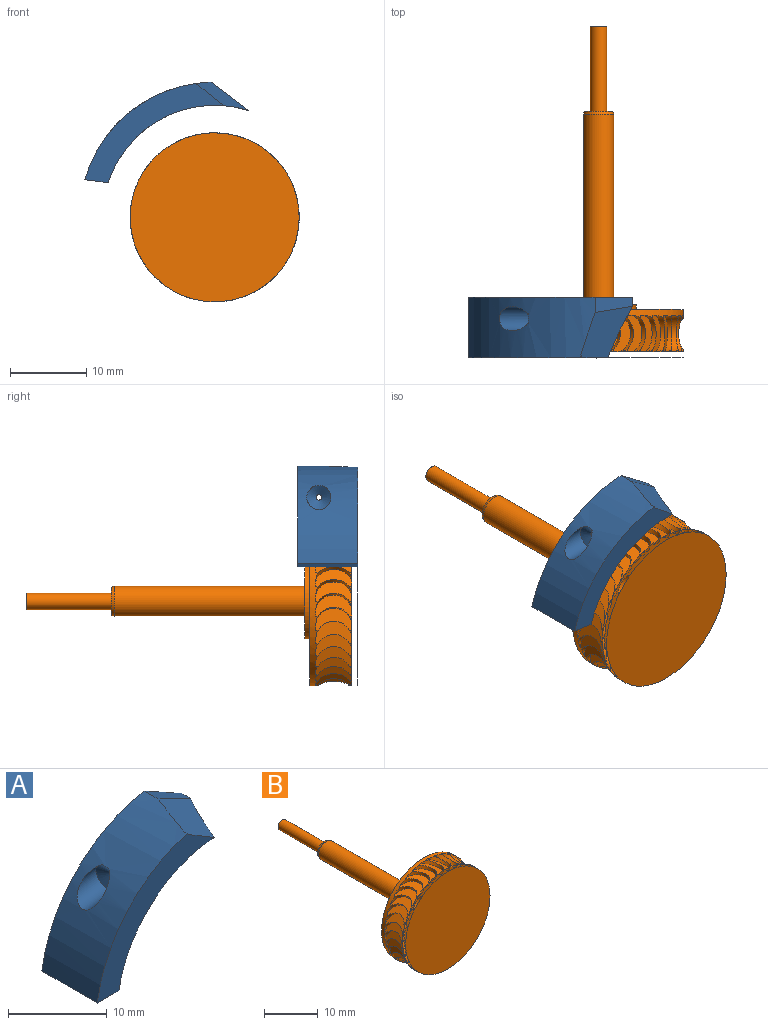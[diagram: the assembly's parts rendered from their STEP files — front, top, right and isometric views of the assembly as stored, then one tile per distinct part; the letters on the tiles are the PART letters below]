
ASSEMBLY  parts=2 mates=2
PART A: 42 faces, bbox 20.2x8.1x15.2 mm
  f0: plane 16.73x14.61mm, normal (0,-1,0), area 61mm2, adj f1,f2,f38,f40,f41
  f1: cylinder r=17.78mm len=15mm, axis (0,1,0), area 159.7mm2, adj f0,f14,f35,f36,f38,f39,f40,f41
  f2: cylinder r=14.73mm len=16.97mm, axis (0,1,0), area 130.5mm2, adj f0,f3,f4,f5,f6,f7,f8,f9
  f3: cylinder r=1.19mm len=0.68mm, axis (0.27,-0.22,0.94), area 0.1mm2, adj f2,f4,f34
  f4: cylinder r=1.19mm len=2.72mm, axis (0.14,-0.22,0.96), area 5.1mm2, adj f2,f3,f34
  f5: cylinder r=1.19mm len=2.42mm, axis (0.27,-0.22,0.94), area 1.4mm2, adj f2,f6,f29,f30
  f6: cylinder r=1.19mm len=0.66mm, axis (0.39,-0.22,0.89), area 0.1mm2, adj f2,f5,f29,f30
  f7: cylinder r=2.39mm len=4.81mm, axis (0.14,-0.22,0.96), area 5.9mm2, adj f2,f30,f31,f32,f33
  f8: cylinder r=1.19mm len=2.42mm, axis (0.39,-0.22,0.89), area 1.4mm2, adj f2,f9,f24,f25
  f9: cylinder r=1.19mm len=0.67mm, axis (0.5,-0.22,0.84), area 0.1mm2, adj f2,f8,f24,f25
  f10: cylinder r=2.39mm len=4.81mm, axis (0.27,-0.22,0.94), area 5.9mm2, adj f2,f25,f26,f27,f28
  f11: cylinder r=1.19mm len=2.42mm, axis (0.5,-0.22,0.84), area 1.4mm2, adj f2,f19,f20
  f12: cylinder r=2.39mm len=4.81mm, axis (0.39,-0.22,0.89), area 5.9mm2, adj f2,f20,f21,f22,f23
  f13: cylinder r=2.39mm len=4.81mm, axis (0.5,-0.22,0.84), area 5.9mm2, adj f2,f15,f16,f17,f18
  f14: plane 20.05x15mm, normal (0,1,0), area 68.5mm2, adj f1,f2,f38,f39
  f15: plane 5.07x5.02mm, normal (-0.5,0.22,-0.84), area 18.8mm2, adj f2,f13,f16,f17
  f16: plane 3.36x1.66mm, normal (0,-0.97,-0.26), area 2.1mm2, adj f2,f13,f15,f19
  f17: plane 1.03x0.51mm, normal (0,0.97,0.26), area 0.2mm2, adj f2,f13,f15
  f18: torus R=2.39mm, axis (-0.87,-0.13,0.48), area 0.7mm2, adj f2,f13,f19
  f19: plane 4.93x3.91mm, normal (0.5,-0.27,0.82), area 8.7mm2, adj f2,f11,f16,f18
  f20: plane 5.31x5.12mm, normal (-0.39,0.22,-0.89), area 15.6mm2, adj f2,f11,f12,f21,f22
  f21: plane 3.46x1.43mm, normal (0.03,-0.97,-0.26), area 2.1mm2, adj f2,f12,f20,f24
  f22: plane 1x0.55mm, normal (-0.03,0.97,0.26), area 0.2mm2, adj f2,f12,f20
  f23: torus R=2.39mm, axis (-0.92,-0.13,0.37), area 0.7mm2, adj f2,f12,f24
  f24: plane 4.9x4.03mm, normal (0.39,-0.27,0.88), area 8.5mm2, adj f2,f8,f9,f21,f23
  f25: plane 5.45x5.1mm, normal (-0.27,0.22,-0.94), area 15.5mm2, adj f2,f8,f9,f10,f26,f27
  f26: plane 3.5x1.23mm, normal (0.07,-0.97,-0.25), area 2.1mm2, adj f2,f10,f25,f29
  f27: plane 0.96x0.57mm, normal (-0.07,0.97,0.25), area 0.2mm2, adj f2,f10,f25
  f28: torus R=2.39mm, axis (-0.96,-0.13,0.24), area 0.7mm2, adj f2,f10,f29
  f29: plane 4.9x4.12mm, normal (0.27,-0.27,0.93), area 8.5mm2, adj f2,f5,f6,f26,f28
  f30: plane 5.51x5.1mm, normal (-0.14,0.22,-0.96), area 15.5mm2, adj f2,f5,f6,f7,f31,f32
  f31: plane 3.48x1mm, normal (0.1,-0.97,-0.24), area 2.1mm2, adj f2,f7,f30,f34
  f32: plane 0.91x0.59mm, normal (-0.1,0.97,0.24), area 0.2mm2, adj f2,f7,f30
  f33: torus R=2.39mm, axis (-0.98,-0.13,0.11), area 0.7mm2, adj f2,f7,f34
  f34: plane 4.9x4.14mm, normal (0.15,-0.27,0.95), area 8.5mm2, adj f2,f3,f4,f31,f33
  f35: cone r=1.59mm half-angle=60deg, axis (-0.99,0,-0.14), area 8.7mm2, adj f1,f36,f37
  f36: cylinder r=1.59mm len=4.17mm, axis (-0.99,0,-0.14), area 19.7mm2, adj f1,f35
  f37: cylinder r=0.36mm len=4.09mm, axis (-0.99,0,-0.14), area 6.9mm2, adj f2,f35
  f38: plane 7.94x3.09mm, normal (0,0,-1), area 24.5mm2, adj f0,f1,f2,f14
  f39: plane 5.4x3.01mm, normal (0.49,0,0.87), area 9.8mm2, adj f1,f2,f14,f41
  f40: plane 0.37x0.12mm, normal (0.87,0.13,-0.48), area 0mm2, adj f0,f1,f41
  f41: plane 7.37x6.91mm, normal (0.5,-0.22,0.84), area 33.6mm2, adj f0,f1,f2,f39,f40
PART B: 156 faces, bbox 67.5x88.1x67.5 mm
  f0: cylinder r=11.11mm len=22.23mm, axis (0,-1,0), area 0.8mm2, adj f1,f47,f48,f49,f50,f51,f52,f53
  f1: plane 49.21x47.21mm, normal (0.34,0,0.94), area 8.1mm2, adj f0,f2,f3,f47,f152,f153
  f2: plane 0.63x0.28mm, normal (0,-1,0), area 0.1mm2, adj f1,f3,f152
  f3: cylinder r=11.11mm len=22.23mm, axis (0,-1,0), area 60.3mm2, adj f1,f2,f4,f5,f6,f7,f8,f9
  f4: plane 0.63x0.28mm, normal (0,-1,0), area 0.1mm2, adj f3,f125,f127
  f5: plane 0.6x0.3mm, normal (0,-1,0), area 0.1mm2, adj f3,f128,f130
  f6: plane 0.56x0.3mm, normal (0,-1,0), area 0.1mm2, adj f3,f131,f133
  f7: plane 0.55x0.39mm, normal (0,-1,0), area 0.1mm2, adj f3,f134,f136
  f8: plane 0.53x0.47mm, normal (0,-1,0), area 0.1mm2, adj f3,f137,f139
  f9: plane 0.54x0.48mm, normal (0,-1,0), area 0.1mm2, adj f3,f140,f142
  f10: plane 0.59x0.43mm, normal (0,-1,0), area 0.1mm2, adj f3,f143,f145
  f11: plane 0.62x0.36mm, normal (0,-1,0), area 0.1mm2, adj f3,f146,f148
  f12: plane 0.63x0.28mm, normal (0,-1,0), area 0.1mm2, adj f3,f149,f151
  f13: plane 0.6x0.3mm, normal (0,-1,0), area 0.1mm2, adj f3,f47,f49
  f14: plane 0.56x0.3mm, normal (0,-1,0), area 0.1mm2, adj f3,f50,f52
  f15: plane 0.55x0.39mm, normal (0,-1,0), area 0.1mm2, adj f3,f53,f55
  f16: plane 0.53x0.47mm, normal (0,-1,0), area 0.1mm2, adj f3,f56,f58
  f17: plane 0.54x0.48mm, normal (0,-1,0), area 0.1mm2, adj f3,f59,f61
  f18: plane 0.59x0.43mm, normal (0,-1,0), area 0.1mm2, adj f3,f62,f64
  f19: plane 0.62x0.36mm, normal (0,-1,0), area 0.1mm2, adj f3,f65,f67
  f20: plane 0.63x0.28mm, normal (0,-1,0), area 0.1mm2, adj f3,f68,f70
  f21: plane 0.63x0.28mm, normal (0,-1,0), area 0.1mm2, adj f3,f71,f73
  f22: plane 0.6x0.3mm, normal (0,-1,0), area 0.1mm2, adj f3,f74,f76
  f23: plane 0.56x0.3mm, normal (0,-1,0), area 0.1mm2, adj f3,f77,f79
  f24: plane 0.55x0.39mm, normal (0,-1,0), area 0.1mm2, adj f3,f80,f82
  f25: plane 0.53x0.47mm, normal (0,-1,0), area 0.1mm2, adj f3,f83,f85
  f26: plane 0.54x0.48mm, normal (0,-1,0), area 0.1mm2, adj f3,f86,f88
  f27: plane 0.59x0.43mm, normal (0,-1,0), area 0.1mm2, adj f3,f89,f91
  f28: plane 0.62x0.36mm, normal (0,-1,0), area 0.1mm2, adj f3,f92,f94
  f29: plane 0.63x0.28mm, normal (0,-1,0), area 0.1mm2, adj f3,f95,f97
  f30: plane 0.63x0.28mm, normal (0,-1,0), area 0.1mm2, adj f3,f98,f100
  f31: plane 0.6x0.3mm, normal (0,-1,0), area 0.1mm2, adj f3,f101,f103
  f32: plane 0.56x0.3mm, normal (0,-1,0), area 0.1mm2, adj f3,f104,f106
  f33: plane 0.55x0.39mm, normal (0,-1,0), area 0.1mm2, adj f3,f107,f109
  f34: plane 0.53x0.47mm, normal (0,-1,0), area 0.1mm2, adj f3,f110,f112
  f35: plane 0.54x0.48mm, normal (0,-1,0), area 0.1mm2, adj f3,f113,f115
  f36: plane 0.59x0.43mm, normal (0,-1,0), area 0.1mm2, adj f3,f116,f118
  f37: plane 0.62x0.36mm, normal (0,-1,0), area 0.1mm2, adj f3,f119,f121
  f38: plane 0.63x0.28mm, normal (0,-1,0), area 0.1mm2, adj f3,f122,f124
  f39: plane 22.23x22.23mm, normal (0,1,0), area 310.9mm2, adj f3,f40
  f40: cylinder r=4.95mm len=9.91mm, axis (0,-1,0), area 19.8mm2, adj f39,f41
  f41: plane 9.91x9.91mm, normal (0,1,0), area 64.7mm2, adj f40,f42
  f42: cylinder r=1.98mm len=25.04mm, axis (0,-1,0), area 311.8mm2, adj f41,f43
  f43: cone r=1.88mm half-angle=14.9deg, axis (0,-1,0), area 4.8mm2, adj f42,f44
  f44: plane 3.76x3.76mm, normal (0,1,0), area 7.4mm2, adj f43,f45
  f45: cylinder r=1.09mm len=11.23mm, axis (0,-1,0), area 77mm2, adj f44,f46
  f46: plane 2.18x2.18mm, normal (0,1,0), area 3.7mm2, adj f45
  f47: cylinder r=2.38mm len=4.76mm, axis (-0.17,0,-0.98), area 4.8mm2, adj f0,f1,f3,f13,f48,f49
  f48: plane 0.6x0.3mm, normal (0,1,0), area 0.1mm2, adj f0,f47,f49
  f49: plane 4.76x2.9mm, normal (0.17,0,0.98), area 8.1mm2, adj f0,f3,f13,f47,f48,f50
  f50: cylinder r=2.38mm len=4.76mm, axis (0,0,-1), area 4.8mm2, adj f0,f3,f14,f49,f51,f52
  f51: plane 0.56x0.3mm, normal (0,1,0), area 0.1mm2, adj f0,f50,f52
  f52: plane 4.76x2.94mm, normal (0,0,1), area 8.1mm2, adj f0,f3,f14,f50,f51,f53
  f53: cylinder r=2.38mm len=4.76mm, axis (0.17,0,-0.98), area 4.8mm2, adj f0,f3,f15,f52,f54,f55
  f54: plane 0.55x0.39mm, normal (0,1,0), area 0.1mm2, adj f0,f53,f55
  f55: plane 4.76x2.9mm, normal (-0.17,0,0.98), area 8.1mm2, adj f0,f3,f15,f53,f54,f56
  f56: cylinder r=2.38mm len=4.76mm, axis (0.34,0,-0.94), area 4.8mm2, adj f0,f3,f16,f55,f57,f58
  f57: plane 0.53x0.47mm, normal (0,1,0), area 0.1mm2, adj f0,f56,f58
  f58: plane 4.76x2.76mm, normal (-0.34,0,0.94), area 8.1mm2, adj f0,f3,f16,f56,f57,f59
  f59: cylinder r=2.38mm len=4.76mm, axis (0.5,0,-0.87), area 4.8mm2, adj f0,f3,f17,f58,f60,f61
  f60: plane 0.54x0.48mm, normal (0,1,0), area 0.1mm2, adj f0,f59,f61
  f61: plane 4.76x2.55mm, normal (-0.5,0,0.87), area 8.1mm2, adj f0,f3,f17,f59,f60,f62
  f62: cylinder r=2.38mm len=4.76mm, axis (0.64,0,-0.77), area 4.8mm2, adj f0,f3,f18,f61,f63,f64
  f63: plane 0.59x0.43mm, normal (0,1,0), area 0.1mm2, adj f0,f62,f64
  f64: plane 4.76x2.25mm, normal (-0.64,0,0.77), area 8.1mm2, adj f0,f3,f18,f62,f63,f65
  f65: cylinder r=2.38mm len=4.76mm, axis (0.77,0,-0.64), area 4.8mm2, adj f0,f3,f19,f64,f66,f67
  f66: plane 0.62x0.36mm, normal (0,1,0), area 0.1mm2, adj f0,f65,f67
  f67: plane 4.76x2.25mm, normal (-0.77,0,0.64), area 8.1mm2, adj f0,f3,f19,f65,f66,f68
  f68: cylinder r=2.38mm len=4.76mm, axis (0.87,0,-0.5), area 4.8mm2, adj f0,f3,f20,f67,f69,f70
  f69: plane 0.63x0.28mm, normal (0,1,0), area 0.1mm2, adj f0,f68,f70
  f70: plane 4.76x2.55mm, normal (-0.87,0,0.5), area 8.1mm2, adj f0,f3,f20,f68,f69,f71
  f71: cylinder r=2.38mm len=4.76mm, axis (0.94,0,-0.34), area 4.8mm2, adj f0,f3,f21,f70,f72,f73
  f72: plane 0.63x0.28mm, normal (0,1,0), area 0.1mm2, adj f0,f71,f73
  f73: plane 4.76x2.76mm, normal (-0.94,0,0.34), area 8.1mm2, adj f0,f3,f21,f71,f72,f74
  f74: cylinder r=2.38mm len=4.76mm, axis (0.98,0,-0.17), area 4.8mm2, adj f0,f3,f22,f73,f75,f76
  f75: plane 0.6x0.3mm, normal (0,1,0), area 0.1mm2, adj f0,f74,f76
  f76: plane 4.76x2.9mm, normal (-0.98,0,0.17), area 8.1mm2, adj f0,f3,f22,f74,f75,f77
  f77: cylinder r=2.38mm len=4.76mm, axis (1,0,0), area 4.8mm2, adj f0,f3,f23,f76,f78,f79
  f78: plane 0.56x0.3mm, normal (0,1,0), area 0.1mm2, adj f0,f77,f79
  f79: plane 4.76x2.94mm, normal (-1,0,0), area 8.1mm2, adj f0,f3,f23,f77,f78,f80
  f80: cylinder r=2.38mm len=4.76mm, axis (0.98,0,0.17), area 4.8mm2, adj f0,f3,f24,f79,f81,f82
  f81: plane 0.55x0.39mm, normal (0,1,0), area 0.1mm2, adj f0,f80,f82
  f82: plane 4.76x2.9mm, normal (-0.98,0,-0.17), area 8.1mm2, adj f0,f3,f24,f80,f81,f83
  f83: cylinder r=2.38mm len=4.76mm, axis (0.94,0,0.34), area 4.8mm2, adj f0,f3,f25,f82,f84,f85
  f84: plane 0.53x0.47mm, normal (0,1,0), area 0.1mm2, adj f0,f83,f85
  f85: plane 4.76x2.76mm, normal (-0.94,0,-0.34), area 8.1mm2, adj f0,f3,f25,f83,f84,f86
  f86: cylinder r=2.38mm len=4.76mm, axis (0.87,0,0.5), area 4.8mm2, adj f0,f3,f26,f85,f87,f88
  f87: plane 0.54x0.48mm, normal (0,1,0), area 0.1mm2, adj f0,f86,f88
  f88: plane 4.76x2.55mm, normal (-0.87,0,-0.5), area 8.1mm2, adj f0,f3,f26,f86,f87,f89
  f89: cylinder r=2.38mm len=4.76mm, axis (0.77,0,0.64), area 4.8mm2, adj f0,f3,f27,f88,f90,f91
  f90: plane 0.59x0.43mm, normal (0,1,0), area 0.1mm2, adj f0,f89,f91
  f91: plane 4.76x2.25mm, normal (-0.77,0,-0.64), area 8.1mm2, adj f0,f3,f27,f89,f90,f92
  f92: cylinder r=2.38mm len=4.76mm, axis (0.64,0,0.77), area 4.8mm2, adj f0,f3,f28,f91,f93,f94
  f93: plane 0.62x0.36mm, normal (0,1,0), area 0.1mm2, adj f0,f92,f94
  f94: plane 4.76x2.25mm, normal (-0.64,0,-0.77), area 8.1mm2, adj f0,f3,f28,f92,f93,f95
  f95: cylinder r=2.38mm len=4.76mm, axis (0.5,0,0.87), area 4.8mm2, adj f0,f3,f29,f94,f96,f97
  f96: plane 0.63x0.28mm, normal (0,1,0), area 0.1mm2, adj f0,f95,f97
  f97: plane 4.76x2.55mm, normal (-0.5,0,-0.87), area 8.1mm2, adj f0,f3,f29,f95,f96,f98
  f98: cylinder r=2.38mm len=4.76mm, axis (0.34,0,0.94), area 4.8mm2, adj f0,f3,f30,f97,f99,f100
  f99: plane 0.63x0.28mm, normal (0,1,0), area 0.1mm2, adj f0,f98,f100
  f100: plane 4.76x2.76mm, normal (-0.34,0,-0.94), area 8.1mm2, adj f0,f3,f30,f98,f99,f101
  f101: cylinder r=2.38mm len=4.76mm, axis (0.17,0,0.98), area 4.8mm2, adj f0,f3,f31,f100,f102,f103
  f102: plane 0.6x0.3mm, normal (0,1,0), area 0.1mm2, adj f0,f101,f103
  f103: plane 4.76x2.9mm, normal (-0.17,0,-0.98), area 8.1mm2, adj f0,f3,f31,f101,f102,f104
  f104: cylinder r=2.38mm len=4.76mm, axis (0,0,1), area 4.8mm2, adj f0,f3,f32,f103,f105,f106
  f105: plane 0.56x0.3mm, normal (0,1,0), area 0.1mm2, adj f0,f104,f106
  f106: plane 4.76x2.94mm, normal (0,0,-1), area 8.1mm2, adj f0,f3,f32,f104,f105,f107
  f107: cylinder r=2.38mm len=4.76mm, axis (-0.17,0,0.98), area 4.8mm2, adj f0,f3,f33,f106,f108,f109
  f108: plane 0.55x0.39mm, normal (0,1,0), area 0.1mm2, adj f0,f107,f109
  f109: plane 4.76x2.9mm, normal (0.17,0,-0.98), area 8.1mm2, adj f0,f3,f33,f107,f108,f110
  f110: cylinder r=2.38mm len=4.76mm, axis (-0.34,0,0.94), area 4.8mm2, adj f0,f3,f34,f109,f111,f112
  f111: plane 0.53x0.47mm, normal (0,1,0), area 0.1mm2, adj f0,f110,f112
  f112: plane 4.76x2.76mm, normal (0.34,0,-0.94), area 8.1mm2, adj f0,f3,f34,f110,f111,f113
  f113: cylinder r=2.38mm len=4.76mm, axis (-0.5,0,0.87), area 4.8mm2, adj f0,f3,f35,f112,f114,f115
  f114: plane 0.54x0.48mm, normal (0,1,0), area 0.1mm2, adj f0,f113,f115
  f115: plane 4.76x2.55mm, normal (0.5,0,-0.87), area 8.1mm2, adj f0,f3,f35,f113,f114,f116
  f116: cylinder r=2.38mm len=4.76mm, axis (-0.64,0,0.77), area 4.8mm2, adj f0,f3,f36,f115,f117,f118
  f117: plane 0.59x0.43mm, normal (0,1,0), area 0.1mm2, adj f0,f116,f118
  f118: plane 4.76x2.25mm, normal (0.64,0,-0.77), area 8.1mm2, adj f0,f3,f36,f116,f117,f119
  f119: cylinder r=2.38mm len=4.76mm, axis (-0.77,0,0.64), area 4.8mm2, adj f0,f3,f37,f118,f120,f121
  f120: plane 0.62x0.36mm, normal (0,1,0), area 0.1mm2, adj f0,f119,f121
  f121: plane 4.76x2.25mm, normal (0.77,0,-0.64), area 8.1mm2, adj f0,f3,f37,f119,f120,f122
  f122: cylinder r=2.38mm len=4.76mm, axis (-0.87,0,0.5), area 4.8mm2, adj f0,f3,f38,f121,f123,f124
  f123: plane 0.63x0.28mm, normal (0,1,0), area 0.1mm2, adj f0,f122,f124
  f124: plane 4.76x2.55mm, normal (0.87,0,-0.5), area 8.1mm2, adj f0,f3,f38,f122,f123,f125
  f125: cylinder r=2.38mm len=4.76mm, axis (-0.94,0,0.34), area 4.8mm2, adj f0,f3,f4,f124,f126,f127
  f126: plane 0.63x0.28mm, normal (0,1,0), area 0.1mm2, adj f0,f125,f127
  f127: plane 4.76x2.76mm, normal (0.94,0,-0.34), area 8.1mm2, adj f0,f3,f4,f125,f126,f128
  f128: cylinder r=2.38mm len=4.76mm, axis (-0.98,0,0.17), area 4.8mm2, adj f0,f3,f5,f127,f129,f130
  f129: plane 0.6x0.3mm, normal (0,1,0), area 0.1mm2, adj f0,f128,f130
  f130: plane 4.76x2.9mm, normal (0.98,0,-0.17), area 8.1mm2, adj f0,f3,f5,f128,f129,f131
  f131: cylinder r=2.38mm len=4.76mm, axis (-1,0,0), area 4.8mm2, adj f0,f3,f6,f130,f132,f133
  f132: plane 0.56x0.3mm, normal (0,1,0), area 0.1mm2, adj f0,f131,f133
  f133: plane 4.76x2.94mm, normal (1,0,0), area 8.1mm2, adj f0,f3,f6,f131,f132,f134
  f134: cylinder r=2.38mm len=4.76mm, axis (-0.98,0,-0.17), area 4.8mm2, adj f0,f3,f7,f133,f135,f136
  f135: plane 0.55x0.39mm, normal (0,1,0), area 0.1mm2, adj f0,f134,f136
  f136: plane 4.76x2.9mm, normal (0.98,0,0.17), area 8.1mm2, adj f0,f3,f7,f134,f135,f137
  f137: cylinder r=2.38mm len=4.76mm, axis (-0.94,0,-0.34), area 4.8mm2, adj f0,f3,f8,f136,f138,f139
  f138: plane 0.53x0.47mm, normal (0,1,0), area 0.1mm2, adj f0,f137,f139
  f139: plane 4.76x2.76mm, normal (0.94,0,0.34), area 8.1mm2, adj f0,f3,f8,f137,f138,f140
  f140: cylinder r=2.38mm len=4.76mm, axis (-0.87,0,-0.5), area 4.8mm2, adj f0,f3,f9,f139,f141,f142
  f141: plane 0.54x0.48mm, normal (0,1,0), area 0.1mm2, adj f0,f140,f142
  f142: plane 4.76x2.55mm, normal (0.87,0,0.5), area 8.1mm2, adj f0,f3,f9,f140,f141,f143
  f143: cylinder r=2.38mm len=4.76mm, axis (-0.77,0,-0.64), area 4.8mm2, adj f0,f3,f10,f142,f144,f145
  f144: plane 0.59x0.43mm, normal (0,1,0), area 0.1mm2, adj f0,f143,f145
  f145: plane 4.76x2.25mm, normal (0.77,0,0.64), area 8.1mm2, adj f0,f3,f10,f143,f144,f146
  f146: cylinder r=2.38mm len=4.76mm, axis (-0.64,0,-0.77), area 4.8mm2, adj f0,f3,f11,f145,f147,f148
  f147: plane 0.62x0.36mm, normal (0,1,0), area 0.1mm2, adj f0,f146,f148
  f148: plane 4.76x2.25mm, normal (0.64,0,0.77), area 8.1mm2, adj f0,f3,f11,f146,f147,f149
  f149: cylinder r=2.38mm len=4.76mm, axis (-0.5,0,-0.87), area 4.8mm2, adj f0,f3,f12,f148,f150,f151
  f150: plane 0.63x0.28mm, normal (0,1,0), area 0.1mm2, adj f0,f149,f151
  f151: plane 4.76x2.55mm, normal (0.5,0,0.87), area 8.1mm2, adj f0,f3,f12,f149,f150,f152
  f152: cylinder r=2.38mm len=4.76mm, axis (-0.34,0,-0.94), area 4.8mm2, adj f0,f1,f2,f3,f151,f153
  f153: plane 45.08x44.73mm, normal (0,1,0), area 0.1mm2, adj f0,f1,f152
  f154: cylinder r=11.11mm len=22.23mm, axis (0,-1,0), area 0mm2, adj f155
  f155: plane 66.68x66.68mm, normal (0,1,0), area 387.9mm2, adj f154
PLACE A rot(axis=(0,1,0),8deg) t=(0,3.18,0)mm
PLACE B at identity
MATE cylindrical B.f0 <-> A.f2  axis (0,-1,0) through (0,0,0)mm
MATE parallel A.f36 <-> B.f133  axis (-1,0,0) through (-8.57,5.13,13.66)mm
